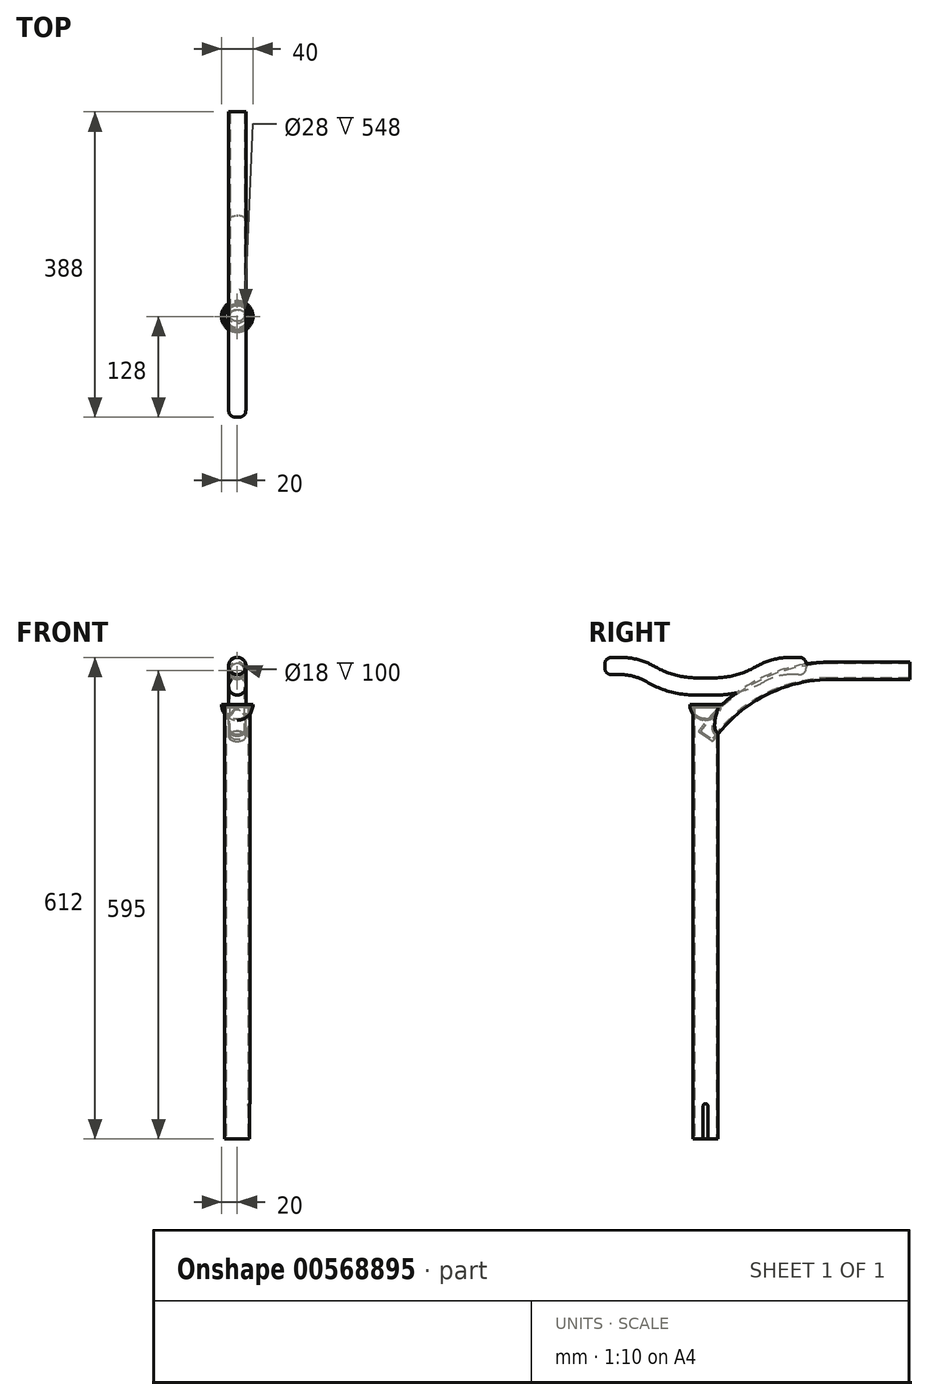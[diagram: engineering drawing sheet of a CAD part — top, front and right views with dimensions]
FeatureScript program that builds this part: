
annotation { "Feature Type Name" : "Feature", "Feature Type Description" : "" }
export const myFeature = defineFeature(function(context is Context, id is Id, definition is map)
    precondition{}
    {
        {
            var Q0;
            Q0=qCreatedBy(makeId("Top.planeOp"),FACE);
            var sketch = newSketch(context, id + "F0", { "sketchPlane" : qUnion([Q0])});
            skCircle(sketch, "E0", {"center": v(0, 0) * mm, "radius": 16 * mm});
            skSolve(sketch);
        }
        {
            var Q0;
            Q0 = qSketchRegion(id + "F0", true);
            extrude(context, id + "F1", {"entities" : qUnion([Q0]), "depth" : 550 * mm, "offsetDistance" : 25 * mm});
        }
        {
            var Q0;
            Q0=makeQuery(id+"F1.opExtrude","CAP_FACE",FACE,{"disambiguationData":[OSD([sQuery(id+"F0.wireOp",EDGE,"E0")])],"isStart":true});
            shell(context, id + "F2", {"entities" : qUnion([Q0]), "thickness" : 2 * mm});
        }
        {
            var Q0;
            Q0=qCreatedBy(makeId("Right.planeOp"),FACE);
            var sketch = newSketch(context, id + "F3", { "sketchPlane" : qUnion([Q0])});
            skLineSegment(sketch, "E1.bottom", {"start": v(-3, 0) * mm, "end": v(3, 0) * mm});
            skLineSegment(sketch, "E1.top", {"start": v(0, 45) * mm, "end": v(0, 45) * mm});
            skLineSegment(sketch, "E1.left", {"start": v(-3, 0) * mm, "end": v(-3, 42) * mm});
            skLineSegment(sketch, "E1.right", {"start": v(3, 0) * mm, "end": v(3, 42) * mm});
            skPoint(sketch, "E2.visualSharp", {"position": v(-3, 45) * mm});
            skArc(sketch, "E2.filletArc", {"start": v(0, 45) * mm, "mid": v(-2.12, 44.12) * mm, "end": v(-3, 42) * mm});
            skPoint(sketch, "E3.visualSharp", {"position": v(3, 45) * mm});
            skArc(sketch, "E3.filletArc", {"start": v(3, 42) * mm, "mid": v(2.12, 44.12) * mm, "end": v(0, 45) * mm});
            skSolve(sketch);
        }
        {
            var Q0;
            Q0 = qSketchRegion(id + "F3", true);
            extrude(context, id + "F4", {"entities" : qUnion([Q0]), "operationType" : NewBodyOperationType.REMOVE, "endBound" : BoundingType.THROUGH_ALL, "depth" : 25 * mm, "offsetDistance" : 25 * mm});
        }
        {
            var Q0;
            Q0=qCreatedBy(makeId("Right.planeOp"),FACE);
            var sketch = newSketch(context, id + "F5", { "sketchPlane" : qUnion([Q0])});
            skArc(sketch, "E4", {"start": v(160, 595) * mm, "mid": v(69.75, 572.86) * mm, "end": v(0, 511.47) * mm});
            skLineSegment(sketch, "E5", {"start": v(160, 595) * mm, "end": v(260, 595) * mm});
            skSolve(sketch);
        }
        {
            var Q0;
            Q0=sQuery(id+"F5.wireOp",VERTEX,"E5.end");
            var Q1;
            Q1=qCreatedBy(makeId("Front.planeOp"),FACE);
            cPlane(context, id + "F6", {"entities" : qUnion([Q0, Q1]), "cplaneType" : CPlaneType.PLANE_POINT, "offset" : 25 * mm, "width" : 150 * mm, "height" : 150 * mm});
        }
        {
            var Q0;
            Q0=qCreatedBy(id+"F6.planeOp",FACE);
            var sketch = newSketch(context, id + "F7", { "sketchPlane" : qUnion([Q0])});
            skCircle(sketch, "E6", {"center": v(0, 595) * mm, "radius": 11 * mm});
            skSolve(sketch);
        }
        {
            var Q0;
            Q0 = qSketchRegion(id + "F7", true);
            var Q1;
            Q1 = qConstructionFilter(qBodyType(qCreatedBy(id + "F5" ,EDGE), BodyType.WIRE), ConstructionObject.NO);
            sweep(context, id + "F8", {"operationType" : NewBodyOperationType.ADD, "profiles" : qUnion([Q0]), "path" : qUnion([Q1])});
        }
        {
            var Q0;
            Q0=makeQuery(id+"F8.opSweep","CAP_FACE",FACE,{"disambiguationData":[OSD([sQuery(id+"F5.wireOp",VERTEX,"E5.end"),sQuery(id+"F7.wireOp",EDGE,"E6")])],"isStart":true});
            shell(context, id + "F9", {"entities" : qUnion([Q0]), "thickness" : 2 * mm});
        }
        {
            var Q0;
            Q0=qCreatedBy(makeId("Right.planeOp"),FACE);
            var sketch = newSketch(context, id + "F10", { "sketchPlane" : qUnion([Q0])});
            skLineSegment(sketch, "E7", {"start": v(0, 575) * mm, "end": v(-12.5, 575) * mm});
            skLineSegment(sketch, "E8", {"start": v(0, 0) * mm, "end": v(0, 575) * mm, "construction": true});
            skArc(sketch, "E9", {"start": v(-69.28, 590.46) * mm, "mid": v(-41.92, 578.93) * mm, "end": v(-12.5, 575) * mm});
            skArc(sketch, "E10", {"start": v(-69.28, 590.46) * mm, "mid": v(-87.93, 598.32) * mm, "end": v(-108, 601) * mm});
            skLineSegment(sketch, "E11", {"start": v(-108, 601) * mm, "end": v(-128, 601) * mm});
            skLineSegment(sketch, "E12.MirrorCS", {"start": v(108, 601) * mm, "end": v(128, 601) * mm});
            skArc(sketch, "E13.MirrorCS", {"start": v(69.28, 590.46) * mm, "mid": v(87.93, 598.32) * mm, "end": v(108, 601) * mm});
            skArc(sketch, "E14.MirrorCS", {"start": v(69.28, 590.46) * mm, "mid": v(41.92, 578.93) * mm, "end": v(12.5, 575) * mm});
            skLineSegment(sketch, "E15.MirrorCS", {"start": v(0, 575) * mm, "end": v(12.5, 575) * mm});
            skSolve(sketch);
        }
        {
            var Q0;
            Q0=sQuery(id+"F10.wireOp",VERTEX,"E12.MirrorCS.end");
            var Q1;
            Q1=qCreatedBy(id+"F6.planeOp",FACE);
            cPlane(context, id + "F11", {"entities" : qUnion([Q0, Q1]), "cplaneType" : CPlaneType.PLANE_POINT, "offset" : 25 * mm, "width" : 150 * mm, "height" : 150 * mm});
        }
        {
            var Q0;
            Q0=qCreatedBy(id+"F11.planeOp",FACE);
            var sketch = newSketch(context, id + "F12", { "sketchPlane" : qUnion([Q0])});
            skCircle(sketch, "E16", {"center": v(0, 601) * mm, "radius": 11 * mm});
            skSolve(sketch);
        }
        {
            var Q0;
            Q0 = qSketchRegion(id + "F12", true);
            var Q1;
            Q1 = qConstructionFilter(qBodyType(qCreatedBy(id + "F10" ,EDGE), BodyType.WIRE), ConstructionObject.NO);
            sweep(context, id + "F13", {"profiles" : qUnion([Q0]), "path" : qUnion([Q1])});
        }
        {
            var Q0;
            Q0=makeQuery(id+"F13.opSweep","CAP_EDGE",EDGE,{"disambiguationData":[OSD([sQuery(id+"F10.wireOp",VERTEX,"E11.end"),sQuery(id+"F12.wireOp",EDGE,"E16")])],"isStart":false});
            var Q1;
            Q1=makeQuery(id+"F13.opSweep","CAP_EDGE",EDGE,{"disambiguationData":[OSD([sQuery(id+"F10.wireOp",VERTEX,"E12.MirrorCS.end"),sQuery(id+"F12.wireOp",EDGE,"E16")])],"isStart":true});
            fillet(context, id + "F14", {"entities" : qUnion([Q0, Q1]), "radius" : 10 * mm, "tangentPropagation" : true, "rho" : 0.5, "crossSection" : FilletCrossSection.CONIC, "allowEdgeOverflow" : false});
        }
        {
            var Q0;
            Q0=qCreatedBy(makeId("Right.planeOp"),FACE);
            var sketch = newSketch(context, id + "F15", { "sketchPlane" : qUnion([Q0])});
            skArc(sketch, "E17", {"start": v(-20, 552) * mm, "mid": v(-14.14, 537.86) * mm, "end": v(0, 532) * mm});
            skLineSegment(sketch, "E18", {"start": v(0, 552) * mm, "end": v(0, 532) * mm});
            skLineSegment(sketch, "E19", {"start": v(0, 552) * mm, "end": v(-20, 552) * mm});
            skSolve(sketch);
        }
        {
            var Q0;
            Q0 = qSketchRegion(id + "F15", true);
            var Q1;
            Q1=sQuery(id+"F15.wireOp",EDGE,"E18");
            revolve(context, id + "F16", {"entities" : qUnion([Q0]), "axis" : qUnion([Q1]), "revolveType" : RevolveType.FULL});
        }
        {
            var Q0;
            Q0=makeQuery(id+"F16.opRevolve","SWEPT_FACE",FACE,{"disambiguationData":[OSD([sQuery(id+"F15.wireOp",EDGE,"E19")])]});
            shell(context, id + "F17", {"entities" : qUnion([Q0]), "thickness" : 2 * mm});
        }
    });
